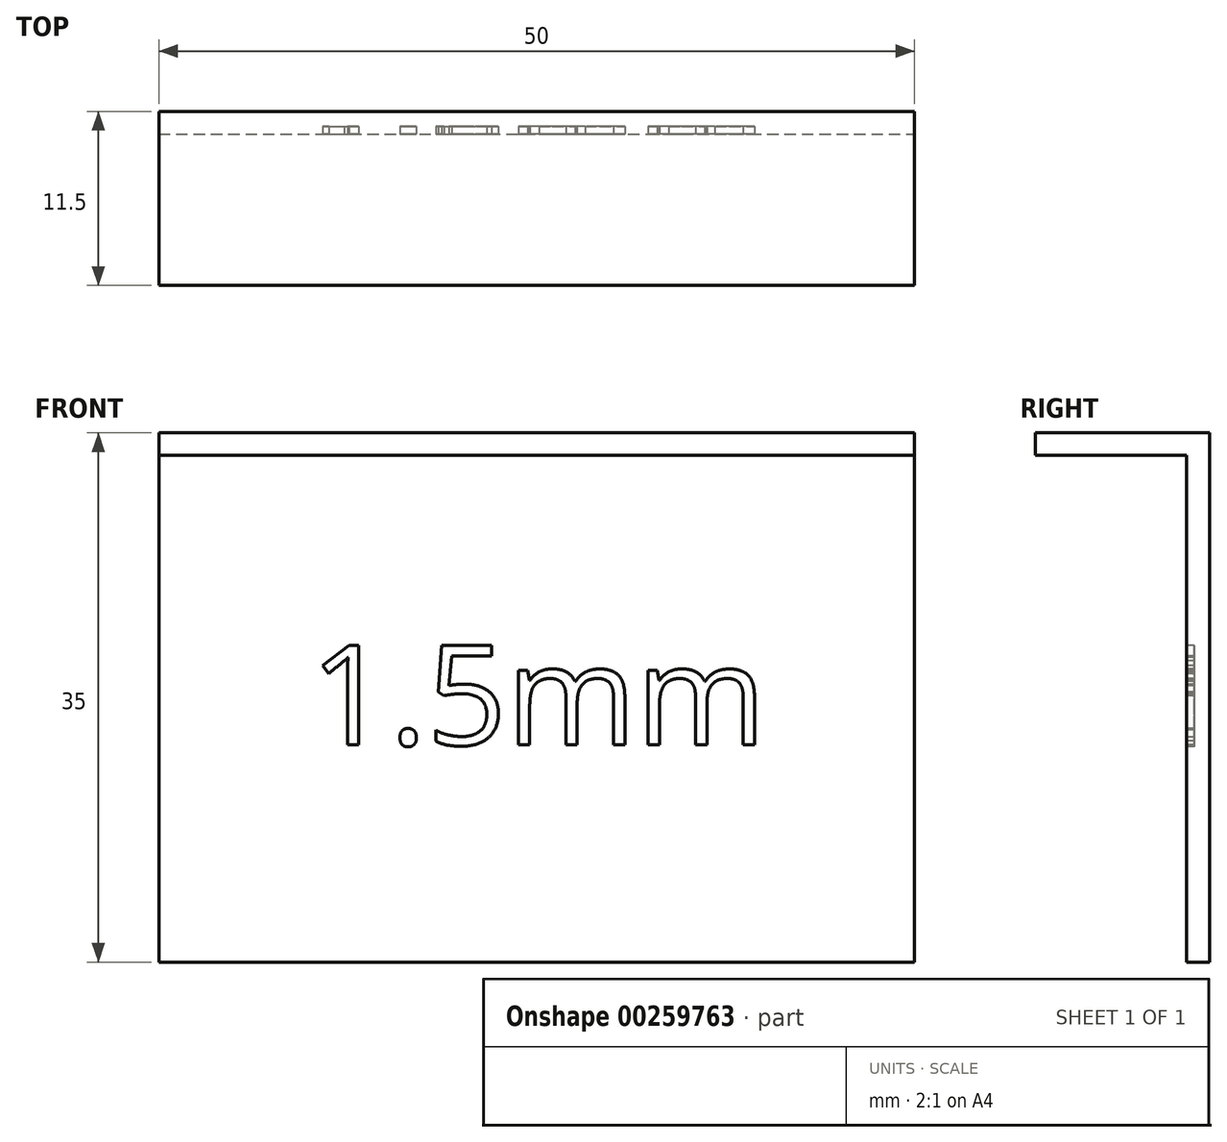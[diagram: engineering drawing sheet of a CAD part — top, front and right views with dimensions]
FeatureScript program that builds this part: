
annotation { "Feature Type Name" : "Feature", "Feature Type Description" : "" }
export const myFeature = defineFeature(function(context is Context, id is Id, definition is map)
    precondition{}
    {
        {
            var Q0;
            Q0=qCreatedBy(makeId("Front.planeOp"),FACE);
            var sketch = newSketch(context, id + "F0", { "sketchPlane" : qUnion([Q0])});
            skLineSegment(sketch, "E0.bottom", {"start": v(-25, 17.5) * mm, "end": v(25, 17.5) * mm});
            skLineSegment(sketch, "E0.top", {"start": v(-25, -17.5) * mm, "end": v(25, -17.5) * mm});
            skLineSegment(sketch, "E0.left", {"start": v(-25, 17.5) * mm, "end": v(-25, -17.5) * mm});
            skLineSegment(sketch, "E0.right", {"start": v(25, 17.5) * mm, "end": v(25, -17.5) * mm});
            skPoint(sketch, "E0.middle", {"position": v(0, 0) * mm});
            skSolve(sketch);
        }
        {
            var Q0;
            Q0 = qSketchRegion(id + "F0", true);
            extrude(context, id + "F1", {"entities" : qUnion([Q0]), "depth" : 1.5 * mm});
        }
        {
            var Q0;
            Q0=makeQuery(id+"F1.opExtrude","CAP_FACE",FACE,{"disambiguationData":[OSD([sQuery(id+"F0.wireOp",EDGE,"E0.bottom"),sQuery(id+"F0.wireOp",EDGE,"E0.top"),sQuery(id+"F0.wireOp",EDGE,"E0.left"),sQuery(id+"F0.wireOp",EDGE,"E0.right")])],"isStart":false});
            var sketch = newSketch(context, id + "F2", { "sketchPlane" : qUnion([Q0])});
            skLineSegment(sketch, "E1.bottom", {"start": v(-25, 17.5) * mm, "end": v(25, 17.5) * mm});
            skLineSegment(sketch, "E1.top", {"start": v(-25, 16) * mm, "end": v(25, 16) * mm});
            skLineSegment(sketch, "E1.left", {"start": v(-25, 17.5) * mm, "end": v(-25, 16) * mm});
            skLineSegment(sketch, "E1.right", {"start": v(25, 17.5) * mm, "end": v(25, 16) * mm});
            skSolve(sketch);
        }
        {
            var Q0;
            Q0 = qSketchRegion(id + "F2", true);
            extrude(context, id + "F3", {"entities" : qUnion([Q0]), "operationType" : NewBodyOperationType.ADD, "depth" : 10 * mm});
        }
        {
            var Q0;
            Q0=makeQuery(id+"F1.opExtrude","CAP_FACE",FACE,{"disambiguationData":[OSD([sQuery(id+"F0.wireOp",EDGE,"E0.bottom"),sQuery(id+"F0.wireOp",EDGE,"E0.top"),sQuery(id+"F0.wireOp",EDGE,"E0.left"),sQuery(id+"F0.wireOp",EDGE,"E0.right")])],"isStart":false});
            var sketch = newSketch(context, id + "F4", { "sketchPlane" : qUnion([Q0])});
            skText(sketch, "E2", { "text": "1.5mm", "fontName": "OpenSans-Regular.ttf"});
            const initialGuessF4  = {"E2": [-0.015, -0.00314, 1, 0, 0.00664]};
            skSetInitialGuess(sketch, initialGuessF4);
            skSolve(sketch);
        }
        {
            var Q0;
            Q0 = qSketchRegion(id + "F4", true);
            extrude(context, id + "F5", {"entities" : qUnion([Q0]), "operationType" : NewBodyOperationType.REMOVE, "oppositeDirection" : true, "depth" : 0.5 * mm});
        }
    });
